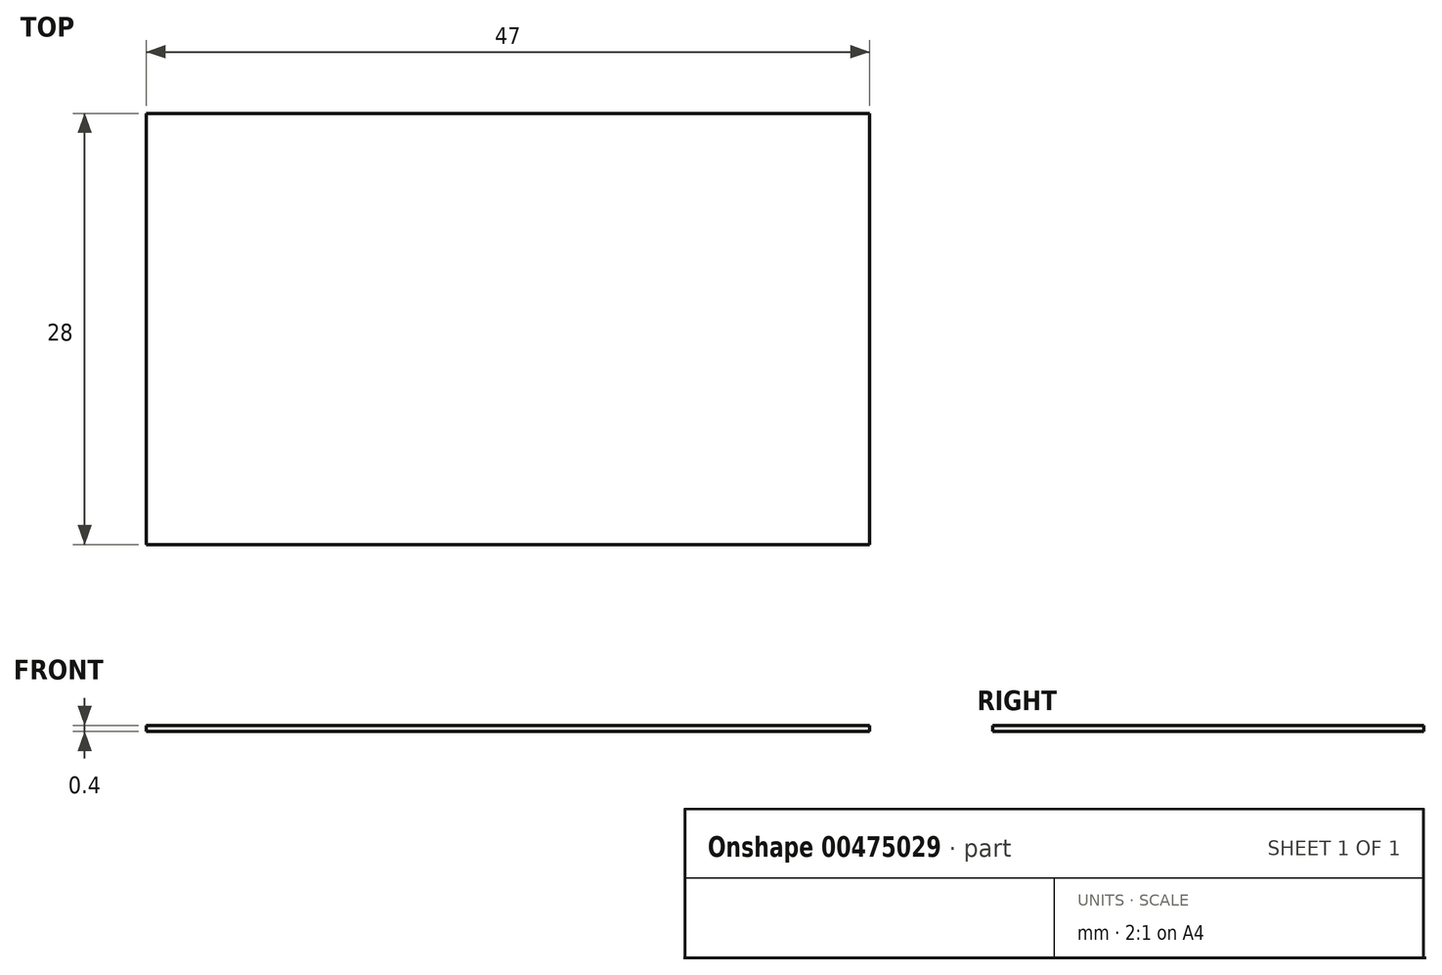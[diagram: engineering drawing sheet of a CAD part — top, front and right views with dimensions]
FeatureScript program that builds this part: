
annotation { "Feature Type Name" : "Feature", "Feature Type Description" : "" }
export const myFeature = defineFeature(function(context is Context, id is Id, definition is map)
    precondition{}
    {
        {
            var Q0;
            Q0=qCreatedBy(makeId("Top.planeOp"),FACE);
            var sketch = newSketch(context, id + "F0", { "sketchPlane" : qUnion([Q0])});
            skLineSegment(sketch, "E0.bottom", {"start": v(-23.5, 14.94) * mm, "end": v(23.5, 14.94) * mm});
            skLineSegment(sketch, "E0.top", {"start": v(-23.5, -13.06) * mm, "end": v(23.5, -13.06) * mm});
            skLineSegment(sketch, "E0.left", {"start": v(-23.5, 14.94) * mm, "end": v(-23.5, -13.06) * mm});
            skLineSegment(sketch, "E0.right", {"start": v(23.5, 14.94) * mm, "end": v(23.5, -13.06) * mm});
            skSolve(sketch);
        }
        {
            var Q0;
            Q0=makeQuery(id+"F0.imprint","IMPRINT",FACE,{"disambiguationData":[TD([[makeQuery(id+"F0.imprint","IMPRINT",EDGE,{"derivedFrom":sQuery(id+"F0.wireOp",EDGE,"E0.bottom")}),-1.0]])]});
            extrude(context, id + "F1", {"entities" : qUnion([Q0]), "depth" : 0.4 * mm});
        }
    });
